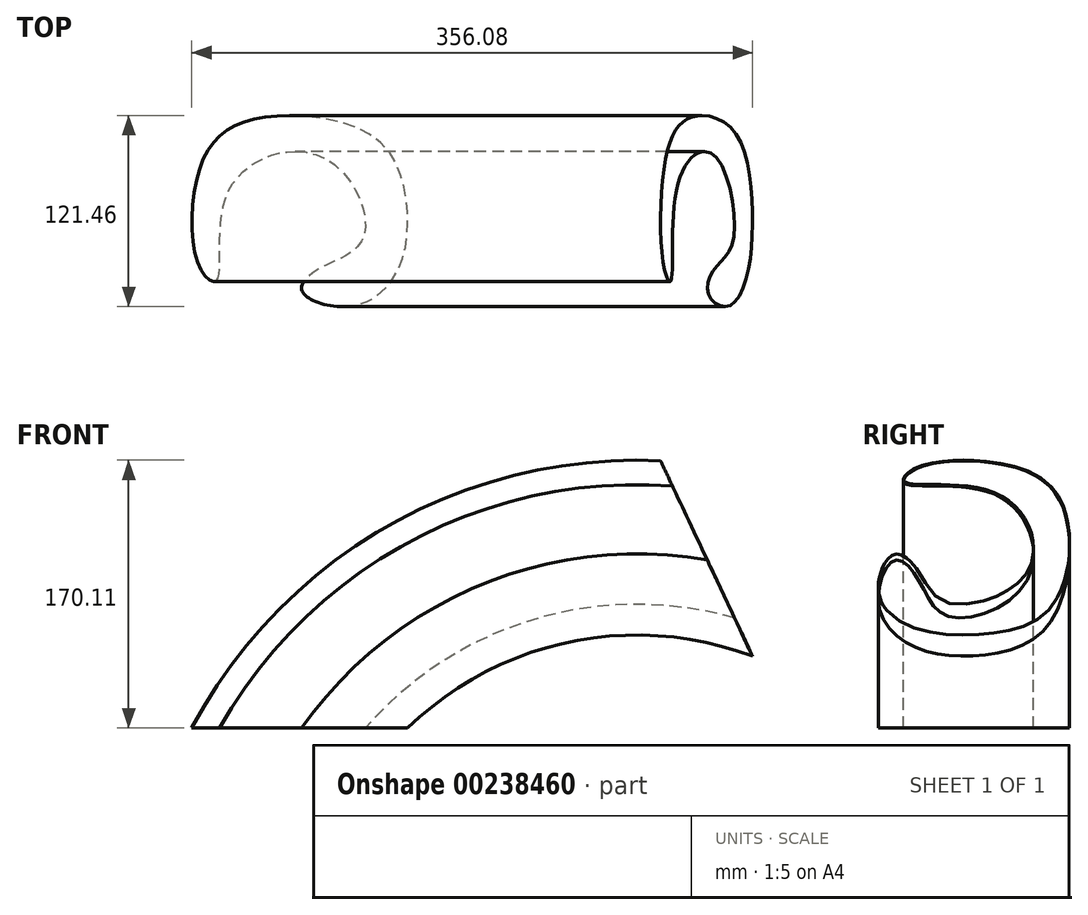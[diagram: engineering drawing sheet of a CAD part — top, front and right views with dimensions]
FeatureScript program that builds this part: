
annotation { "Feature Type Name" : "Feature", "Feature Type Description" : "" }
export const myFeature = defineFeature(function(context is Context, id is Id, definition is map)
    precondition{}
    {
        {
            var Q0;
            Q0=qCreatedBy(makeId("Top.planeOp"),FACE);
            var sketch = newSketch(context, id + "F0", { "sketchPlane" : qUnion([Q0])});
            skFitSpline(sketch, "E0", {"points": [v(-54.35, -57.24) * mm, v(-46.48, 0) * mm, v(13.92, 20.48) * mm, v(39.12, -29.4) * mm, v(11.82, -49.37) * mm, v(0, -64.07) * mm, v(32.3, -73.52) * mm, v(61.18, -49.9) * mm, v(66.43, -9.45) * mm, v(46.48, 33.09) * mm, v(-28.1, 45.69) * mm, v(-63.8, 17.33) * mm, v(-64.86, -49.37) * mm, v(-54.35, -57.24) * mm]});
            skSolve(sketch);
        }
        {
            var Q0;
            Q0=qCreatedBy(makeId("Front.planeOp"),FACE);
            var sketch = newSketch(context, id + "F1", { "sketchPlane" : qUnion([Q0])});
            skArc(sketch, "E1", {"start": v(257.45, 106.33) * mm, "mid": v(113.28, 90.56) * mm, "end": v(0, 0) * mm});
            skSolve(sketch);
        }
        {
            var Q0;
            Q0=makeQuery(id+"F0.imprint","IMPRINT",FACE,{"disambiguationData":[TD([[makeQuery(id+"F0.imprint","IMPRINT",EDGE,{"derivedFrom":sQuery(id+"F0.wireOp",EDGE,"E0")}),1.0]])]});
            var Q1;
            Q1=sQuery(id+"F0.wireOp",EDGE,"E0");
            var Q2;
            Q2=sQuery(id+"F1.wireOp",EDGE,"E1");
            sweep(context, id + "F2", {"bodyType" : ToolBodyType.SURFACE, "profiles" : qUnion([Q0]), "surfaceProfiles" : qUnion([Q1]), "path" : qUnion([Q2])});
        }
    });
